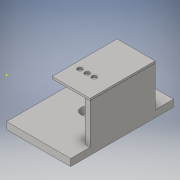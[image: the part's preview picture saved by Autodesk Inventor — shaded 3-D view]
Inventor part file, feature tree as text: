
AUTODESK INVENTOR PART (.ipt)
format: ipt  version: 2016 (Build 200138000, 138)  size: 124,928 bytes
history: native  units: in
note: dims shown in document units (in); Inventor stores cm internally (conversion verified against a paired STEP export)
features: sketch x4, hole x4, extrude x3
ambient origin geometry x8: Origin, YZ Plane, XZ Plane, XY Plane, X Axis, Y Axis, Z Axis, Center Point
bodies: Solid1 (feature_tree)
feature tree (11):
  extrude  "Extrusion1"  Depth=1.5748in TaperAngle=0.0deg
  extrude  "Extrusion2"  Depth=0.0787in
  sketch  "Sketch3"  dims[d10=0.19in d11=0.75in d12=0.119in d13=0.25in d14=0.5635in d15=1.6in d16=0.0in d17=0.0in]
  extrude  "Extrusion3"  TaperAngle=0.0deg  [1 undecoded]
  hole  "Hole1"  [1 undecoded]
  hole  "Hole2"  [1 undecoded]
  hole  "Hole3"  [1 undecoded]
  hole  "Hole4"  [1 undecoded]
  sketch  "Sketch1"  dims[d2=0.2756in d3=0.0in d4=1.5748in d5=0.0in]
  sketch  "Sketch2"  dims[d6=0.0787in d7=0.0in d8=1.0in d9=1.0in]
  sketch  "Sketch4"  dims[d18=0.0in d19=1.0in d20=1.0in d21=0.19in d22=0.75in d23=0.375in d24=0.25in d25=0.5635in d26=0.1875in d27=0.0in d28=1.0in d29=1.0in d30=0.19in d31=0.75in d32=0.375in d33=0.25in d34=0.5635in d35=0.1875in d36=0.0in d37=0.1969in d48=0.3937in d49=0.3937in d41=0.5in d42=0.2362in d43=0.1575in d44=0.0787in d45=90.0deg d46=0.3041in d47=0.0in]
note: 5 required parameter values undecoded (feature->parameter linkage not recoverable at this tier; creation-order binding heuristic only, values carry confidence <= 0.55)
